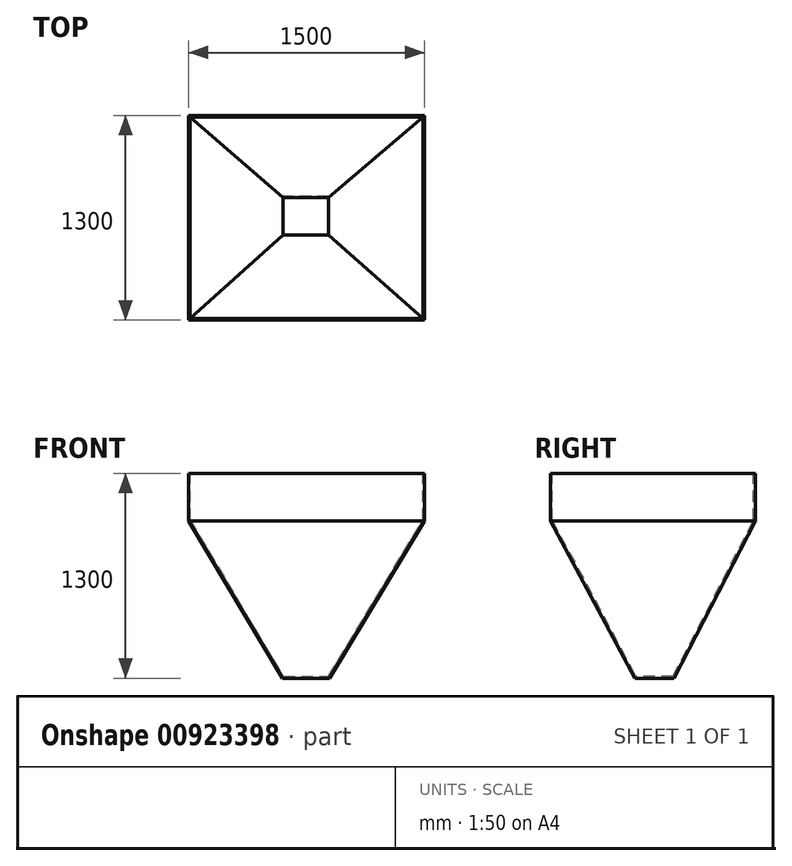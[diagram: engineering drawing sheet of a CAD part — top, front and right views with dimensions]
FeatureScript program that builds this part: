
annotation { "Feature Type Name" : "Feature", "Feature Type Description" : "" }
export const myFeature = defineFeature(function(context is Context, id is Id, definition is map)
    precondition{}
    {
        {
            var Q0;
            Q0=qCreatedBy(makeId("Top.planeOp"),FACE);
            var sketch = newSketch(context, id + "F0", { "sketchPlane" : qUnion([Q0])});
            skLineSegment(sketch, "E0.bottom", {"start": v(-747.14, 621.75) * mm, "end": v(752.86, 621.75) * mm});
            skLineSegment(sketch, "E0.top", {"start": v(-747.14, -678.25) * mm, "end": v(752.86, -678.25) * mm});
            skLineSegment(sketch, "E0.left", {"start": v(-747.14, 621.75) * mm, "end": v(-747.14, -678.25) * mm});
            skLineSegment(sketch, "E0.right", {"start": v(752.86, 621.75) * mm, "end": v(752.86, -678.25) * mm});
            skSolve(sketch);
        }
        {
            var Q0;
            Q0=makeQuery(id+"F0.imprint","IMPRINT",FACE,{"disambiguationData":[TD([[makeQuery(id+"F0.imprint","IMPRINT",EDGE,{"derivedFrom":sQuery(id+"F0.wireOp",EDGE,"E0.bottom")}),-1.0]])]});
            extrude(context, id + "F1", {"entities" : qUnion([Q0]), "oppositeDirection" : true, "depth" : 300 * mm, "offsetDistance" : 25.4 * mm});
        }
        {
            var Q0;
            Q0=qCreatedBy(makeId("Top.planeOp"),FACE);
            cPlane(context, id + "F2", {"entities" : qUnion([Q0]), "cplaneType" : CPlaneType.OFFSET, "offset" : 1300 * mm, "oppositeDirection" : true, "width" : 152.4 * mm, "height" : 152.4 * mm});
        }
        {
            var Q0;
            Q0=qCreatedBy(id+"F2.planeOp",FACE);
            var sketch = newSketch(context, id + "F3", { "sketchPlane" : qUnion([Q0])});
            skLineSegment(sketch, "E1.bottom", {"start": v(149.3, -143.34) * mm, "end": v(-150.7, -143.34) * mm});
            skLineSegment(sketch, "E1.top", {"start": v(149.3, 106.66) * mm, "end": v(-150.7, 106.66) * mm});
            skLineSegment(sketch, "E1.left", {"start": v(149.3, -143.34) * mm, "end": v(149.3, 106.66) * mm});
            skLineSegment(sketch, "E1.right", {"start": v(-150.7, -143.34) * mm, "end": v(-150.7, 106.66) * mm});
            skSolve(sketch);
        }
        {
            var Q0;
            Q0=makeQuery(id+"F1.opExtrude","CAP_FACE",FACE,{"disambiguationData":[OSD([sQuery(id+"F0.wireOp",EDGE,"E0.bottom"),sQuery(id+"F0.wireOp",EDGE,"E0.top"),sQuery(id+"F0.wireOp",EDGE,"E0.left"),sQuery(id+"F0.wireOp",EDGE,"E0.right")])],"isStart":false});
            var sketch = newSketch(context, id + "F4", { "sketchPlane" : qUnion([Q0])});
            skLineSegment(sketch, "E2.bottom", {"start": v(752.86, 678.25) * mm, "end": v(-747.14, 678.25) * mm});
            skLineSegment(sketch, "E2.top", {"start": v(752.86, -621.75) * mm, "end": v(-747.14, -621.75) * mm});
            skLineSegment(sketch, "E2.left", {"start": v(752.86, 678.25) * mm, "end": v(752.86, -621.75) * mm});
            skLineSegment(sketch, "E2.right", {"start": v(-747.14, 678.25) * mm, "end": v(-747.14, -621.75) * mm});
            skSolve(sketch);
        }
        {
            var Q1;
            Q1=makeQuery(id+"F4.imprint","IMPRINT",FACE,{"disambiguationData":[TD([[makeQuery(id+"F4.imprint","IMPRINT",EDGE,{"derivedFrom":sQuery(id+"F4.wireOp",EDGE,"E2.bottom")}),-1.0]])]});
            var Q2;
            Q2=makeQuery(id+"F3.imprint","IMPRINT",FACE,{"disambiguationData":[TD([[makeQuery(id+"F3.imprint","IMPRINT",EDGE,{"derivedFrom":sQuery(id+"F3.wireOp",EDGE,"E1.bottom")}),-1.0]])]});
            loft(context, id + "F5", {"operationType" : NewBodyOperationType.ADD, "sheetProfilesArray" : [{ "sheetProfileEntities" : qUnion([Q1]) }, { "sheetProfileEntities" : qUnion([Q2]) }]});
        }
        {
            var Q0;
            Q0=makeQuery(id+"F1.opExtrude","CAP_FACE",FACE,{"disambiguationData":[OSD([sQuery(id+"F0.wireOp",EDGE,"E0.bottom"),sQuery(id+"F0.wireOp",EDGE,"E0.top"),sQuery(id+"F0.wireOp",EDGE,"E0.left"),sQuery(id+"F0.wireOp",EDGE,"E0.right")])],"isStart":true});
            var Q1;
            Q1=makeQuery(id+"F5.opLoft","CAP_FACE",FACE,{"disambiguationData":[OSD([makeQuery(id+"F3.imprint","IMPRINT",FACE,{"disambiguationData":[TD([[makeQuery(id+"F3.imprint","IMPRINT",EDGE,{"derivedFrom":sQuery(id+"F3.wireOp",EDGE,"E1.bottom")}),-1.0]])]})])],"isStart":true});
            shell(context, id + "F6", {"entities" : qUnion([Q0, Q1]), "thickness" : 10 * mm});
        }
    });
